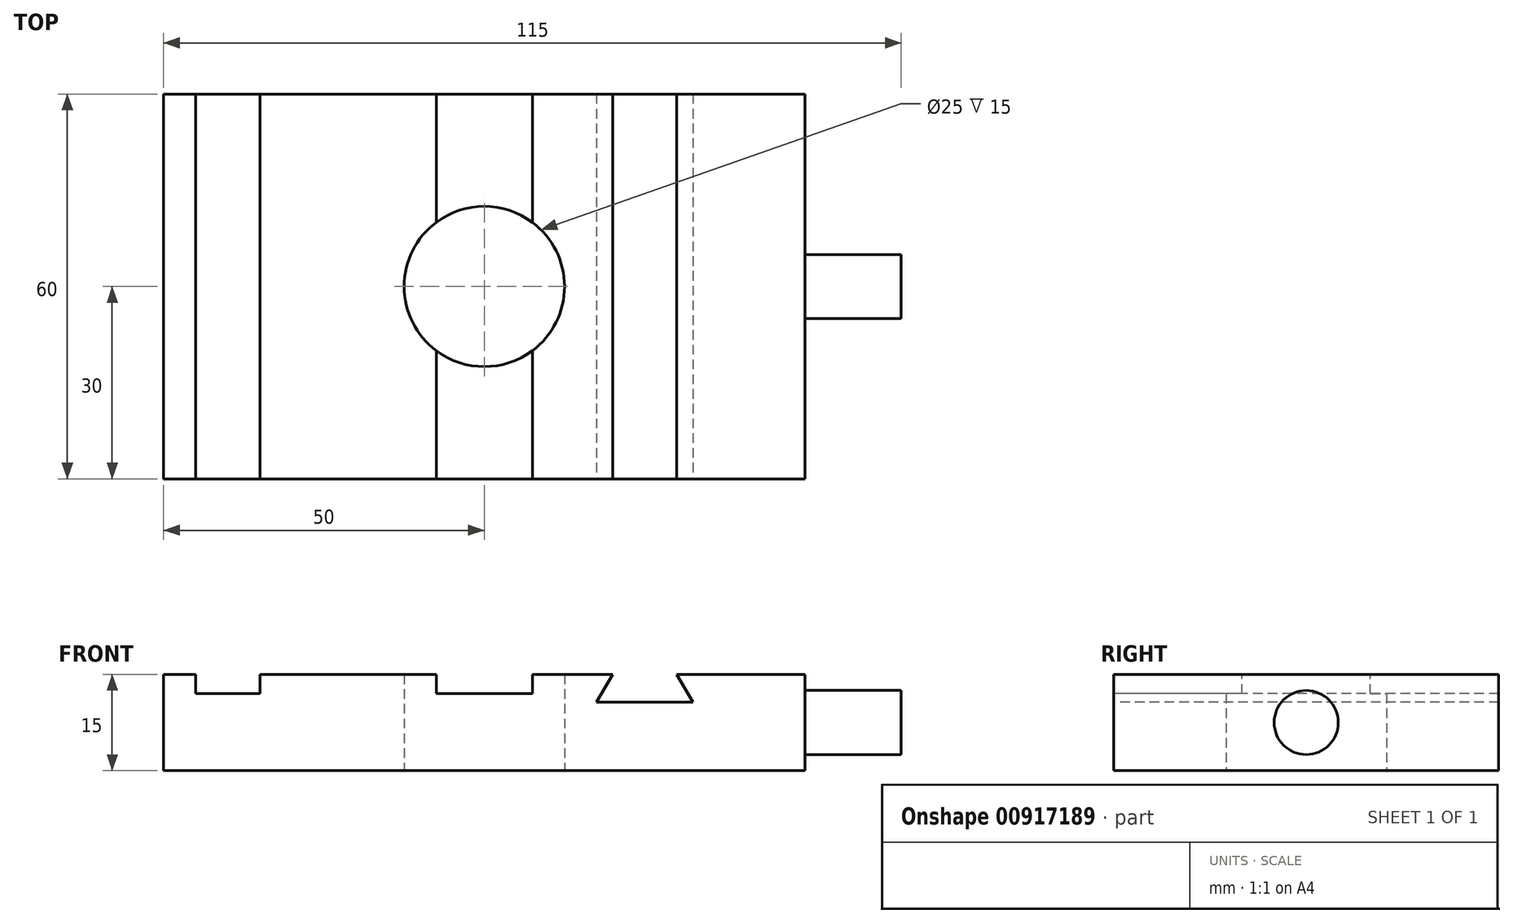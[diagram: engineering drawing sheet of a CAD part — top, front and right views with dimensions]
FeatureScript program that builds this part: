
annotation { "Feature Type Name" : "Feature", "Feature Type Description" : "" }
export const myFeature = defineFeature(function(context is Context, id is Id, definition is map)
    precondition{}
    {
        {
            var Q0;
            Q0=qCreatedBy(makeId("Top.planeOp"),FACE);
            var sketch = newSketch(context, id + "F0", { "sketchPlane" : qUnion([Q0])});
            skLineSegment(sketch, "E0.bottom", {"start": v(50, -30) * mm, "end": v(-50, -30) * mm});
            skLineSegment(sketch, "E0.top", {"start": v(50, 30) * mm, "end": v(-50, 30) * mm});
            skLineSegment(sketch, "E0.left", {"start": v(50, -30) * mm, "end": v(50, 30) * mm});
            skLineSegment(sketch, "E0.right", {"start": v(-50, -30) * mm, "end": v(-50, 30) * mm});
            skPoint(sketch, "E0.middle", {"position": v(0, 0) * mm});
            skCircle(sketch, "E1", {"center": v(0, 0) * mm, "radius": 12.5 * mm});
            skSolve(sketch);
        }
        {
            var Q0;
            Q0=makeQuery(id+"F0.imprint","IMPRINT",FACE,{"disambiguationData":[TD([[makeQuery(id+"F0.imprint","IMPRINT",EDGE,{"derivedFrom":sQuery(id+"F0.wireOp",EDGE,"E0.bottom")}),-1.0]])]});
            extrude(context, id + "F1", {"entities" : qUnion([Q0]), "depth" : 15 * mm, "offsetDistance" : 25 * mm});
        }
        {
            var Q0;
            Q0=makeQuery(id+"F1.opExtrude","CAP_FACE",FACE,{"disambiguationData":[OSD([sQuery(id+"F0.wireOp",EDGE,"E0.bottom"),sQuery(id+"F0.wireOp",EDGE,"E0.top"),sQuery(id+"F0.wireOp",EDGE,"E0.left"),sQuery(id+"F0.wireOp",EDGE,"E0.right"),sQuery(id+"F0.wireOp",EDGE,"E1")])],"isStart":false});
            var sketch = newSketch(context, id + "F2", { "sketchPlane" : qUnion([Q0])});
            skLineSegment(sketch, "E2.bottom", {"start": v(-45, 30) * mm, "end": v(-35, 30) * mm});
            skLineSegment(sketch, "E2.top", {"start": v(-45, -30) * mm, "end": v(-35, -30) * mm});
            skLineSegment(sketch, "E2.left", {"start": v(-45, 30) * mm, "end": v(-45, -30) * mm});
            skLineSegment(sketch, "E2.right", {"start": v(-35, 30) * mm, "end": v(-35, -30) * mm});
            skLineSegment(sketch, "E3", {"start": v(-7.5, 30) * mm, "end": v(-7.5, -30) * mm});
            skLineSegment(sketch, "E4", {"start": v(-7.5, -30) * mm, "end": v(7.5, -30) * mm});
            skLineSegment(sketch, "E5", {"start": v(7.5, -30) * mm, "end": v(7.5, 30) * mm});
            skLineSegment(sketch, "E6", {"start": v(7.5, 30) * mm, "end": v(-7.5, 30) * mm});
            skLineSegment(sketch, "E7", {"start": v(0, 30) * mm, "end": v(0, -30) * mm, "construction": true});
            skSolve(sketch);
        }
        {
            var Q0;
            {var subQ0=sQuery(id+"F2.wireOp",EDGE,"E6");Q0=makeQuery(id+"F2.imprint","IMPRINT",FACE,{"disambiguationData":[TD([[makeQuery(id+"F2.imprint","IMPRINT",EDGE,{"derivedFrom":subQ0}),1.0]])]});}
            var Q1;
            {var subQ0=sQuery(id+"F2.wireOp",EDGE,"E4");Q1=makeQuery(id+"F2.imprint","IMPRINT",FACE,{"disambiguationData":[TD([[makeQuery(id+"F2.imprint","IMPRINT",EDGE,{"derivedFrom":subQ0}),-1.0]])]});}
            var Q2;
            Q2=makeQuery(id+"F2.imprint","IMPRINT",FACE,{"disambiguationData":[TD([[makeQuery(id+"F2.imprint","IMPRINT",EDGE,{"derivedFrom":sQuery(id+"F2.wireOp",EDGE,"E2.bottom")}),1.0]])]});
            extrude(context, id + "F3", {"entities" : qUnion([Q0, Q1, Q2]), "operationType" : NewBodyOperationType.REMOVE, "oppositeDirection" : true, "depth" : 3 * mm, "offsetDistance" : 25 * mm});
        }
        {
            var Q0;
            Q0=makeQuery(id+"F1.opExtrude","SWEPT_FACE",FACE,{"disambiguationData":[OSD([sQuery(id+"F0.wireOp",EDGE,"E0.bottom")])]});
            var sketch = newSketch(context, id + "F4", { "sketchPlane" : qUnion([Q0])});
            skLineSegment(sketch, "E8", {"start": v(20, 15) * mm, "end": v(17.5, 10.67) * mm});
            skLineSegment(sketch, "E9", {"start": v(17.5, 10.67) * mm, "end": v(32.5, 10.67) * mm});
            skLineSegment(sketch, "E10", {"start": v(32.5, 10.67) * mm, "end": v(30, 15) * mm});
            skLineSegment(sketch, "E11", {"start": v(30, 15) * mm, "end": v(20, 15) * mm});
            skLineSegment(sketch, "E12", {"start": v(25, 10.67) * mm, "end": v(25, 15) * mm, "construction": true});
            skSolve(sketch);
        }
        {
            var Q0;
            Q0=makeQuery(id+"F4.imprint","IMPRINT",FACE,{"disambiguationData":[TD([[makeQuery(id+"F4.imprint","IMPRINT",EDGE,{"derivedFrom":sQuery(id+"F4.wireOp",EDGE,"E8")}),1.0]])]});
            extrude(context, id + "F5", {"entities" : qUnion([Q0]), "operationType" : NewBodyOperationType.REMOVE, "endBound" : BoundingType.THROUGH_ALL, "oppositeDirection" : true, "depth" : 25 * mm, "offsetDistance" : 25 * mm});
        }
        {
            var Q0;
            Q0=makeQuery(id+"F1.opExtrude","SWEPT_FACE",FACE,{"disambiguationData":[OSD([sQuery(id+"F0.wireOp",EDGE,"E0.left")])]});
            var sketch = newSketch(context, id + "F6", { "sketchPlane" : qUnion([Q0])});
            skCircle(sketch, "E13", {"center": v(0, 7.5) * mm, "radius": 5 * mm});
            skPoint(sketch, "E13.centerSnap0", {"position": v(0, 15) * mm});
            skPoint(sketch, "E13.centerSnap1", {"position": v(30, 7.5) * mm});
            skSolve(sketch);
        }
        {
            var Q0;
            Q0=makeQuery(id+"F6.imprint","IMPRINT",FACE,{"disambiguationData":[TD([[makeQuery(id+"F6.imprint","IMPRINT",EDGE,{"derivedFrom":sQuery(id+"F6.wireOp",EDGE,"E13")}),1.0]])]});
            extrude(context, id + "F7", {"entities" : qUnion([Q0]), "operationType" : NewBodyOperationType.ADD, "depth" : 15 * mm, "offsetDistance" : 25 * mm});
        }
    });
